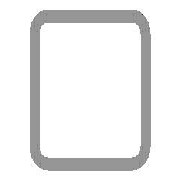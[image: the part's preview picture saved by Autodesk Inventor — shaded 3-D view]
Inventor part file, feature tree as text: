
AUTODESK INVENTOR PART (.ipt)
format: ipt  version: 2025.1 (Build 291241020, 241B)  size: 135,680 bytes
history: native  units: mm (DEFAULTED — no unit token found)
features: other x4, sketch x1, plane x1
ambient origin geometry x8: Origin, YZ Plane, XZ Plane, XY Plane, X Axis, Y Axis, Z Axis, Center Point
bodies: Solid1 (feature_tree), Body (feature_tree)
feature tree (6):
  parser-record x1  (decoder bookkeeping rows leaked as tree rows — omitted from the tree; the rows remain in map.json)
  other  "Driven Length"
  other  "Start Plane"
  other  "End Plane"
  sketch  "Sketch3"  dims[d3=1710.0mm d4=0.0mm d7=4.5mm d10=80.0mm d11=80.0mm d12=3.0mm d13=-0.0mm d14=1710.0mm d15=40.0mm d16=40.0mm d17=90.0deg d18=1710.0mm]
  plane  "Work Plane3"
